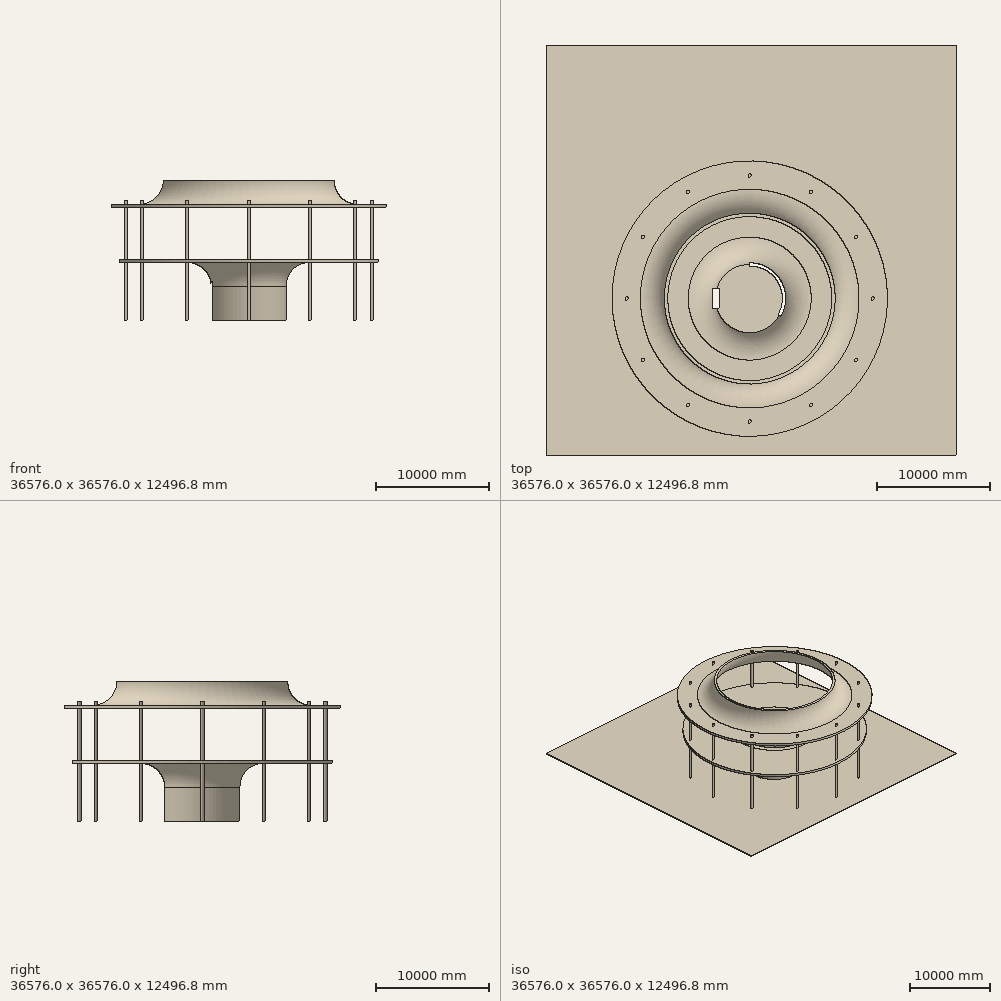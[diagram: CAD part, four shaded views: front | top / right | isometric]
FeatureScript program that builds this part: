
annotation { "Feature Type Name" : "Feature", "Feature Type Description" : "" }
export const myFeature = defineFeature(function(context is Context, id is Id, definition is map)
    precondition{}
    {
        {
            var Q0;
            Q0=qCreatedBy(makeId("Top.planeOp"),FACE);
            var sketch = newSketch(context, id + "F0", { "sketchPlane" : qUnion([Q0])});
            skLineSegment(sketch, "E0.bottom", {"start": v(-18133.34, 22583.62) * mm, "end": v(18442.66, 22583.62) * mm});
            skLineSegment(sketch, "E0.top", {"start": v(-18133.34, -13992.38) * mm, "end": v(18442.66, -13992.38) * mm});
            skLineSegment(sketch, "E0.left", {"start": v(-18133.34, 22583.62) * mm, "end": v(-18133.34, -13992.38) * mm});
            skLineSegment(sketch, "E0.right", {"start": v(18442.66, 22583.62) * mm, "end": v(18442.66, -13992.38) * mm});
            skSolve(sketch);
        }
        {
            var Q0;
            Q0=makeQuery(id+"F0.imprint","IMPRINT",FACE,{"disambiguationData":[TD([[makeQuery(id+"F0.imprint","IMPRINT",EDGE,{"derivedFrom":sQuery(id+"F0.wireOp",EDGE,"E0.bottom")}),-1.0]])]});
            extrude(context, id + "F1", {"entities" : qUnion([Q0]), "depth" : 30.48 * mm, "offsetDistance" : 30.48 * mm});
        }
        {
            var Q0;
            Q0=qCreatedBy(makeId("Right.planeOp"),FACE);
            var sketch = newSketch(context, id + "F2", { "sketchPlane" : qUnion([Q0])});
            skLineSegment(sketch, "E1.bottom", {"start": v(3048, 0) * mm, "end": v(3352.8, 0) * mm});
            skLineSegment(sketch, "E1.top", {"start": v(3048, 3048) * mm, "end": v(3352.8, 3048) * mm});
            skLineSegment(sketch, "E1.left", {"start": v(3048, 0) * mm, "end": v(3048, 3048) * mm});
            skLineSegment(sketch, "E1.right", {"start": v(3352.8, 0) * mm, "end": v(3352.8, 3048) * mm});
            skArc(sketch, "E2", {"start": v(5486.4, 5181.6) * mm, "mid": v(3977.72, 4556.68) * mm, "end": v(3352.8, 3048) * mm});
            skArc(sketch, "E3", {"start": v(5486.4, 5486.4) * mm, "mid": v(3762.2, 4772.2) * mm, "end": v(3048, 3048) * mm});
            skLineSegment(sketch, "E4", {"start": v(5486.4, 5486.4) * mm, "end": v(5486.4, 5181.6) * mm});
            skLineSegment(sketch, "E5.bottom", {"start": v(5486.4, 5486.4) * mm, "end": v(11582.4, 5486.4) * mm});
            skLineSegment(sketch, "E5.top", {"start": v(5486.4, 5181.6) * mm, "end": v(11582.4, 5181.6) * mm});
            skLineSegment(sketch, "E5.right", {"start": v(11582.4, 5486.4) * mm, "end": v(11582.4, 5181.6) * mm});
            skLineSegment(sketch, "E6", {"start": v(0, 9157.5) * mm, "end": v(0, -356.14) * mm, "construction": true});
            skSolve(sketch);
        }
        {
            var Q0;
            Q0=makeQuery(id+"F2.imprint","IMPRINT",FACE,{"disambiguationData":[TD([[makeQuery(id+"F2.imprint","IMPRINT",EDGE,{"derivedFrom":sQuery(id+"F2.wireOp",EDGE,"E1.bottom")}),1.0]])]});
            var Q1;
            Q1=makeQuery(id+"F2.imprint","IMPRINT",FACE,{"disambiguationData":[TD([[makeQuery(id+"F2.imprint","IMPRINT",EDGE,{"derivedFrom":sQuery(id+"F2.wireOp",EDGE,"E1.top")}),1.0]])]});
            var Q2;
            Q2=makeQuery(id+"F2.imprint","IMPRINT",FACE,{"disambiguationData":[TD([[makeQuery(id+"F2.imprint","IMPRINT",EDGE,{"derivedFrom":sQuery(id+"F2.wireOp",EDGE,"E5.bottom")}),-1.0]])]});
            var Q3;
            Q3=sQuery(id+"F2.wireOp",EDGE,"E6");
            revolve(context, id + "F3", {"operationType" : NewBodyOperationType.ADD, "entities" : qUnion([Q0, Q1, Q2]), "axis" : qUnion([Q3]), "revolveType" : RevolveType.FULL});
        }
        {
            var Q0;
            {var subQ0=sQuery(id+"F0.wireOp",EDGE,"E0.left");var subQ1=sQuery(id+"F0.wireOp",EDGE,"E0.top");var subQ2=sQuery(id+"F0.wireOp",EDGE,"E0.right");var subQ3=sQuery(id+"F0.wireOp",EDGE,"E0.bottom");Q0=makeQuery(id+"F3.boolean.opBoolean","SPLIT",FACE,{"disambiguationData":[TD([makeQuery(id+"F1.opExtrude","SWEPT_FACE",FACE,{"disambiguationData":[OSD([subQ3])]})])],"derivedFrom":makeQuery(id+"F1.opExtrude","CAP_FACE",FACE,{"disambiguationData":[OSD([subQ3,subQ1,subQ0,subQ2])],"isStart":false})});}
            var sketch = newSketch(context, id + "F4", { "sketchPlane" : qUnion([Q0])});
            skLineSegment(sketch, "E7", {"start": v(0, 0) * mm, "end": v(0, 15958.42) * mm, "construction": true});
            skCircle(sketch, "E8", {"center": v(0, 10972.8) * mm, "radius": 152.4 * mm});
            skCircle(sketch, "E9.1.0", {"center": v(-5486.4, 9502.72) * mm, "radius": 152.4 * mm});
            skCircle(sketch, "E9.2.0", {"center": v(-9502.72, 5486.4) * mm, "radius": 152.4 * mm});
            skPoint(sketch, "E9.center", {"position": v(0, 0) * mm});
            skCircle(sketch, "E10", {"center": v(0, 0) * mm, "radius": 10972.8 * mm, "construction": true});
            skPoint(sketch, "E11.center", {"position": v(9502.72, 16459.2) * mm});
            skLineSegment(sketch, "E11.anchor1", {"start": v(9502.72, 16459.2) * mm, "end": v(0, 10972.8) * mm, "construction": true});
            skLineSegment(sketch, "E11.anchor2", {"start": v(9502.72, 16459.2) * mm, "end": v(0, 10972.8) * mm, "construction": true});
            skCircle(sketch, "E12.1.3.0", {"center": v(-10972.8, 0) * mm, "radius": 152.4 * mm});
            skCircle(sketch, "E12.1.4.0", {"center": v(-9502.72, -5486.4) * mm, "radius": 152.4 * mm});
            skCircle(sketch, "E12.1.5.0", {"center": v(-5486.4, -9502.72) * mm, "radius": 152.4 * mm});
            skCircle(sketch, "E12.1.6.0", {"center": v(0, -10972.8) * mm, "radius": 152.4 * mm});
            skCircle(sketch, "E12.1.7.0", {"center": v(5486.4, -9502.72) * mm, "radius": 152.4 * mm});
            skCircle(sketch, "E12.1.8.0", {"center": v(9502.72, -5486.4) * mm, "radius": 152.4 * mm});
            skCircle(sketch, "E12.1.9.0", {"center": v(10972.8, 0) * mm, "radius": 152.4 * mm});
            skCircle(sketch, "E12.1.10.0", {"center": v(9502.72, 5486.4) * mm, "radius": 152.4 * mm});
            skCircle(sketch, "E12.1.11.0", {"center": v(5486.4, 9502.72) * mm, "radius": 152.4 * mm});
            skSolve(sketch);
        }
        {
            var Q0;
            Q0 = qSketchRegion(id + "F4", true);
            extrude(context, id + "F5", {"entities" : qUnion([Q0]), "operationType" : NewBodyOperationType.ADD, "depth" : 10668 * mm, "offsetDistance" : 30.48 * mm});
        }
        {
            var Q0;
            Q0=makeQuery(id+"F2.imprint","IMPRINT",FACE,{"disambiguationData":[TD([[makeQuery(id+"F2.imprint","IMPRINT",EDGE,{"derivedFrom":sQuery(id+"F2.wireOp",EDGE,"E1.bottom")}),1.0]])]});
            var sketch = newSketch(context, id + "F6", { "sketchPlane" : qUnion([Q0])});
            skLineSegment(sketch, "E13", {"start": v(0, 0) * mm, "end": v(0, 17308.4) * mm, "construction": true});
            skLineSegment(sketch, "E14", {"start": v(9753.6, 10363.2) * mm, "end": v(9753.6, 10058.4) * mm});
            skArc(sketch, "E15", {"start": v(7620, 12496.8) * mm, "mid": v(8244.92, 10988.12) * mm, "end": v(9753.6, 10363.2) * mm});
            skArc(sketch, "E16", {"start": v(7315.2, 12496.8) * mm, "mid": v(8029.4, 10772.6) * mm, "end": v(9753.6, 10058.4) * mm});
            skLineSegment(sketch, "E17", {"start": v(7315.2, 12496.8) * mm, "end": v(7620, 12496.8) * mm});
            skLineSegment(sketch, "E18.bottom", {"start": v(9753.6, 10363.2) * mm, "end": v(12286.1, 10363.2) * mm});
            skLineSegment(sketch, "E18.top", {"start": v(9753.6, 10058.4) * mm, "end": v(12286.1, 10058.4) * mm});
            skLineSegment(sketch, "E18.right", {"start": v(12286.1, 10363.2) * mm, "end": v(12286.1, 10058.4) * mm});
            skLineSegment(sketch, "E19", {"start": v(9753.6, 10058.4) * mm, "end": v(9753.6, 14684.83) * mm, "construction": true});
            skSolve(sketch);
        }
        {
            var Q0;
            Q0=makeQuery(id+"F6.imprint","IMPRINT",FACE,{"disambiguationData":[TD([[makeQuery(id+"F6.imprint","IMPRINT",EDGE,{"derivedFrom":sQuery(id+"F6.wireOp",EDGE,"E15")}),-1.0]])]});
            var Q1;
            Q1=makeQuery(id+"F6.imprint","IMPRINT",FACE,{"disambiguationData":[TD([[makeQuery(id+"F6.imprint","IMPRINT",EDGE,{"derivedFrom":sQuery(id+"F6.wireOp",EDGE,"E18.bottom")}),-1.0]])]});
            var Q2;
            Q2=sQuery(id+"F6.wireOp",EDGE,"E13");
            revolve(context, id + "F7", {"entities" : qUnion([Q0, Q1]), "axis" : qUnion([Q2]), "revolveType" : RevolveType.FULL});
        }
        {
            var Q0;
            Q0=makeQuery(id+"F3.opRevolve","SWEPT_FACE",FACE,{"disambiguationData":[OSD([sQuery(id+"F2.wireOp",EDGE,"E5.bottom")])]});
            var sketch = newSketch(context, id + "F8", { "sketchPlane" : qUnion([Q0])});
            skLineSegment(sketch, "E20.bottom", {"start": v(-3352.8, -914.4) * mm, "end": v(-2743.2, -914.4) * mm});
            skLineSegment(sketch, "E20.top", {"start": v(-3352.8, 914.4) * mm, "end": v(-2743.2, 914.4) * mm});
            skLineSegment(sketch, "E20.left", {"start": v(-2743.2, -914.4) * mm, "end": v(-2743.2, 914.4) * mm});
            skLineSegment(sketch, "E20.right", {"start": v(-3352.8, -914.4) * mm, "end": v(-3352.8, 914.4) * mm});
            skLineSegment(sketch, "E21", {"start": v(0, 0) * mm, "end": v(-1076.53, 0) * mm, "construction": true});
            skArc(sketch, "E22", {"start": v(2543.4, -1419.53) * mm, "mid": v(2511.84, 1474.66) * mm, "end": v(0, 2912.72) * mm});
            skArc(sketch, "E23", {"start": v(2781.19, -1590.2) * mm, "mid": v(2771.12, 1607.67) * mm, "end": v(0, 3203.7) * mm});
            skLineSegment(sketch, "E24", {"start": v(0, 2912.72) * mm, "end": v(0, 3203.7) * mm});
            skLineSegment(sketch, "E25", {"start": v(2543.4, -1419.53) * mm, "end": v(2781.19, -1590.2) * mm});
            skSolve(sketch);
        }
        {
            var Q0;
            Q0=makeQuery(id+"F8.imprint","IMPRINT",FACE,{"disambiguationData":[TD([[makeQuery(id+"F8.imprint","IMPRINT",EDGE,{"derivedFrom":sQuery(id+"F8.wireOp",EDGE,"E20.bottom")}),1.0]])]});
            var Q1;
            Q1=makeQuery(id+"F8.imprint","IMPRINT",FACE,{"disambiguationData":[TD([[makeQuery(id+"F8.imprint","IMPRINT",EDGE,{"derivedFrom":sQuery(id+"F8.wireOp",EDGE,"E22")}),-1.0]])]});
            extrude(context, id + "F9", {"entities" : qUnion([Q0, Q1]), "operationType" : NewBodyOperationType.REMOVE, "oppositeDirection" : true, "depth" : 6096 * mm, "offsetDistance" : 30.48 * mm});
        }
    });
